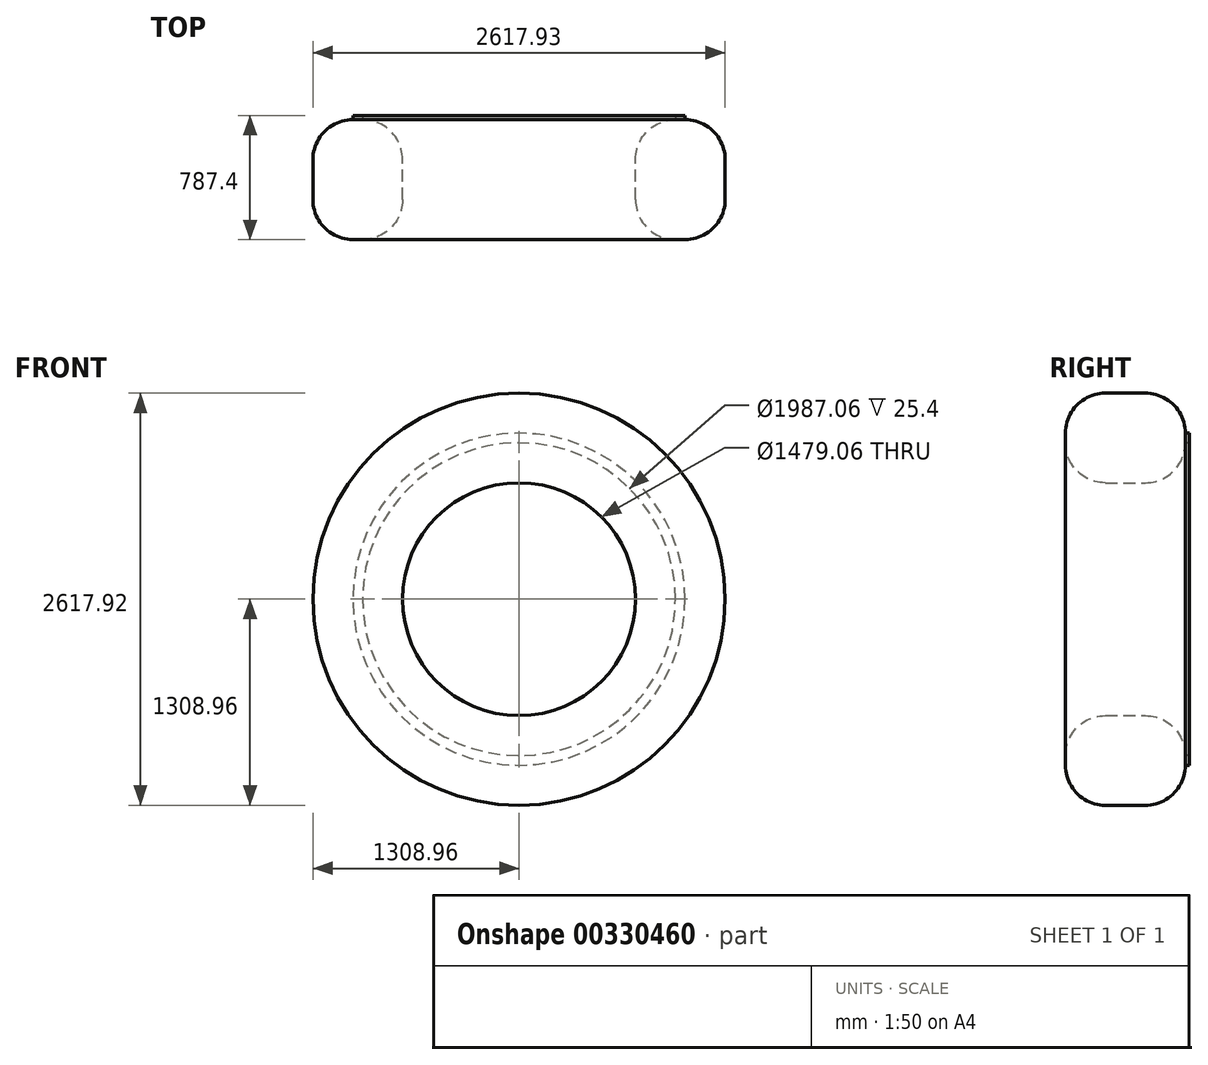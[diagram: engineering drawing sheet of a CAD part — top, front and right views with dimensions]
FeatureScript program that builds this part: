
annotation { "Feature Type Name" : "Feature", "Feature Type Description" : "" }
export const myFeature = defineFeature(function(context is Context, id is Id, definition is map)
    precondition{}
    {
        {
            var Q0;
            Q0=qCreatedBy(makeId("Front.planeOp"),FACE);
            var sketch = newSketch(context, id + "F0", { "sketchPlane" : qUnion([Q0])});
            skCircle(sketch, "E0", {"center": v(-20.15, 0) * mm, "radius": 1308.96 * mm});
            skCircle(sketch, "E1", {"center": v(-20.15, 0) * mm, "radius": 739.53 * mm});
            skSolve(sketch);
        }
        {
            var Q0;
            Q0 = qSketchRegion(id + "F0", true);
            extrude(context, id + "F1", {"entities" : qUnion([Q0]), "depth" : 762 * mm});
        }
        {
            var Q0;
            Q0=makeQuery(id+"F1.opExtrude","CAP_EDGE",EDGE,{"disambiguationData":[OSD([sQuery(id+"F0.wireOp",EDGE,"E0")])],"isStart":true});
            fillet(context, id + "F2", {"entities" : qUnion([Q0]), "radius" : 254 * mm, "tangentPropagation" : true, "allowEdgeOverflow" : false});
        }
        {
            var Q0;
            Q0=makeQuery(id+"F1.opExtrude","CAP_FACE",FACE,{"disambiguationData":[OSD([sQuery(id+"F0.wireOp",EDGE,"E0"),sQuery(id+"F0.wireOp",EDGE,"E1")])],"isStart":false});
            fillet(context, id + "F3", {"entities" : qUnion([Q0]), "radius" : 254 * mm, "tangentPropagation" : true, "allowEdgeOverflow" : false});
        }
        {
            var Q0;
            Q0=makeQuery(id+"F1.opExtrude","SWEPT_FACE",FACE,{"disambiguationData":[OSD([sQuery(id+"F0.wireOp",EDGE,"E1")])]});
            var Q1;
            {var subQ0=sQuery(id+"F0.wireOp",EDGE,"E0");Q1=makeQuery(id+"F3.opFillet","BLEND_EDGE",EDGE,{"blendedFrom":[makeQuery(id+"F1.opExtrude","CAP_EDGE",EDGE,{"disambiguationData":[OSD([subQ0])],"isStart":false}),makeQuery(id+"F1.opExtrude","CAP_FACE",FACE,{"disambiguationData":[OSD([subQ0,sQuery(id+"F0.wireOp",EDGE,"E1")])],"isStart":false})],"blendedInto":[makeQuery(id+"F1.opExtrude","CAP_FACE",FACE,{"disambiguationData":[OSD([subQ0,sQuery(id+"F0.wireOp",EDGE,"E1")])],"isStart":false})]});}
            var Q2;
            {var subQ0=sQuery(id+"F0.wireOp",EDGE,"E1");Q2=makeQuery(id+"F3.opFillet","BLEND_EDGE",EDGE,{"blendedFrom":[makeQuery(id+"F1.opExtrude","CAP_EDGE",EDGE,{"disambiguationData":[OSD([subQ0])],"isStart":false}),makeQuery(id+"F1.opExtrude","CAP_FACE",FACE,{"disambiguationData":[OSD([sQuery(id+"F0.wireOp",EDGE,"E0"),subQ0])],"isStart":false})],"blendedInto":[makeQuery(id+"F1.opExtrude","CAP_FACE",FACE,{"disambiguationData":[OSD([sQuery(id+"F0.wireOp",EDGE,"E0"),subQ0])],"isStart":false})]});}
            var Q3;
            Q3=makeQuery(id+"F1.opExtrude","SWEPT_FACE",FACE,{"disambiguationData":[OSD([sQuery(id+"F0.wireOp",EDGE,"E0")])]});
            fillet(context, id + "F4", {"entities" : qUnion([Q0, Q1, Q2, Q3]), "radius" : 254 * mm, "tangentPropagation" : true, "allowEdgeOverflow" : false});
        }
        {
            var Q0;
            Q0=makeQuery(id+"F1.opExtrude","CAP_FACE",FACE,{"disambiguationData":[OSD([sQuery(id+"F0.wireOp",EDGE,"E0"),sQuery(id+"F0.wireOp",EDGE,"E1")])],"isStart":true});
            extrude(context, id + "F5", {"entities" : qUnion([Q0]), "depth" : 25.4 * mm});
        }
    });
